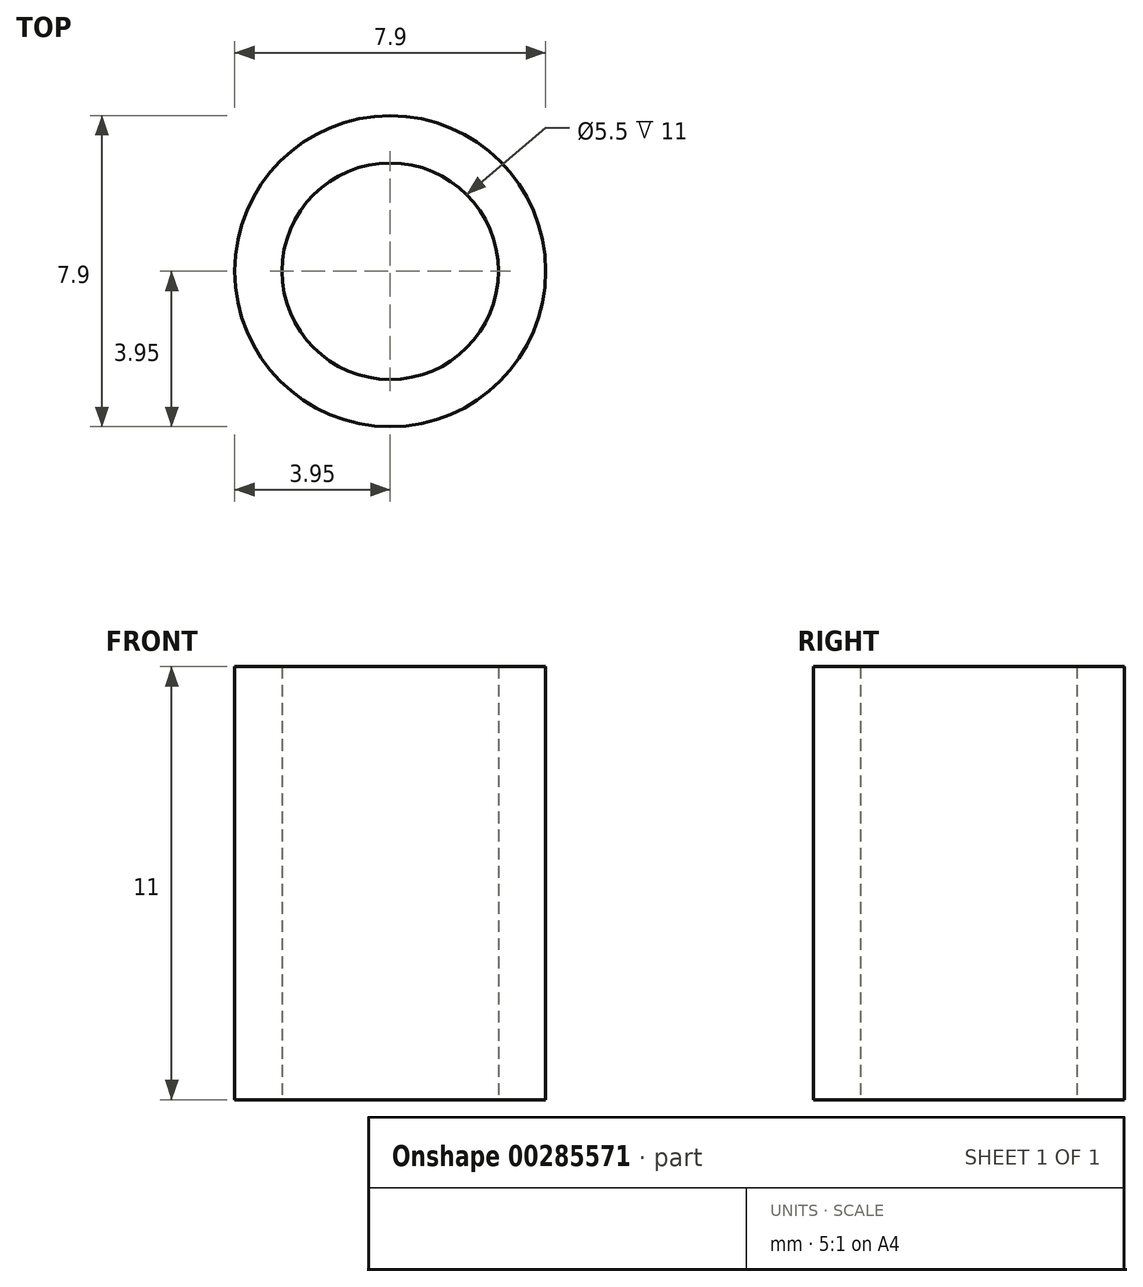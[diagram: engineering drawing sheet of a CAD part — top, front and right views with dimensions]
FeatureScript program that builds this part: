
annotation { "Feature Type Name" : "Feature", "Feature Type Description" : "" }
export const myFeature = defineFeature(function(context is Context, id is Id, definition is map)
    precondition{}
    {
        {
            var Q0;
            Q0=qCreatedBy(makeId("Top.planeOp"),FACE);
            var sketch = newSketch(context, id + "F0", { "sketchPlane" : qUnion([Q0])});
            skCircle(sketch, "E0", {"center": v(0, 0) * mm, "radius": 2.75 * mm});
            skCircle(sketch, "E1.0", {"center": v(0, 0) * mm, "radius": 3.95 * mm});
            skSolve(sketch);
        }
        {
            var Q0;
            Q0 = qSketchRegion(id + "F0", true);
            extrude(context, id + "F1", {"entities" : qUnion([Q0]), "depth" : (35 - 14 - 10) * mm});
        }
    });
